# Revit family: 02_HSMAGIS40-52_A
name_source: partatom
category: Porte
units: mm (PartAtom-declared; Revit-internal decimal feet)

## family parameters
Condiviso = No
Host = Muro
Numero OmniClass = 23.30.10.00
Punto di calcolo locali = Sì
Sempre verticale = Sì
Taglio con vuoti quando caricato = No
Titolo OmniClass = Doors

## types (2) — shared parameters
Altezza = 2000 mm  [stored 6.56168 ft]
Chiusura muro = Per host
Codice assieme = B2030100
Costruzione analitica = <Nessuno>
EXTERNAL ALUMINUM FRAME/TELAIO ALLUMINIO ESTERNO = UNIFORM_ALUMINUM
GLASS WEIGHT/PESO VETRO = 43.00 kg/m²
H = 2000 mm  [stored 6.56168 ft]
HANDLE HEIGHT/ALTEZZA MANIGLIA = 1100 mm  [stored 3.60892 ft]
HANDLE/MANIGLIA = UNIFORM_ALUMINUM
INTERIOR WOOD FRAME/TELAIO LEGNO INTERNO = UNIFORM_WOOD
Larghezza = 1500 mm  [stored 4.92126 ft]
Larghezza telaio = 75 mm  [stored 0.246063 ft]
MAXIMUM HEIGHT/ALTEZZA MASSIMA = 3200 mm  [stored 10.4987 ft]
MAXIMUM WIDTH/LARGHEZZA MASSIMA = 9009 mm
MAX_DIMENSIONS_WARNING = No
MINIMUM HEIGHT/ALTEZZA MINIMA = 1200 mm
MINIMUM WIDTH/LARGHEZZA MINIMA  = 1200 mm
Modello = HSMAGIS
PRODUCER WEBSITE/SITO WEB PRODUTTORE = www.uniform.it
PRODUCT WEBSITE/SITO WEB PRODOTTO = www.sistema-uni-one.it
Proiezione telaio est. = 25 mm  [stored 0.082021 ft]
Proiezione telaio int. = 25 mm  [stored 0.082021 ft]
VOID = 1955 mm  [stored 6.41404 ft]
WINDOW GLASS/VETRO FINESTRA = UNIFORM_GLASS
zero-valued in all types: Rw GLASS/Rw VETRO, Rw WINDOW/Rw FINESTRA

## per-type parameters (varying)
| type | D1 | D2 | DIM1_anta scorrevole | DIM2_vetro fisso | Ug GLASS/Ug VETRO | Uw WINDOW/Uw FINESTRA | W |
| THERMAL | 800 mm  [stored 2.62467 ft] | 800 mm  [stored 2.62467 ft] | 800 mm  [stored 2.62467 ft] | 800 mm  [stored 2.62467 ft] | 1.0000 W/(m²·K) | 1.3000 W/(m²·K) | 1609 mm  [stored 5.27887 ft] |
| THERMAL_PERFORMANCE | 1000 mm  [stored 3.28084 ft] | 1100 mm  [stored 3.60892 ft] | 1000 mm  [stored 3.28084 ft] | 1100 mm  [stored 3.60892 ft] | 0.5000 W/(m²·K) | 0.8500 W/(m²·K) | 2109 mm  [stored 6.91929 ft] |

note: [stored X ft] marks values corroborated as IEEE doubles in the binary element streams (Revit-internal decimal feet)
